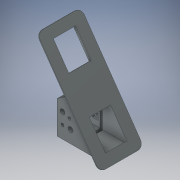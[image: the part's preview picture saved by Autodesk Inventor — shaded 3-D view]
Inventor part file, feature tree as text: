
AUTODESK INVENTOR PART (.ipt)
format: ipt  version: 2017 (Build 210142000, 142)  size: 451,072 bytes
history: native  units: mm
features: extrude x25, sketch x24, other x16, reference x6, fillet x2, hole x2, projected_geometry x2, shell x1
ambient origin geometry x8: Origin, YZ Plane, XZ Plane, XY Plane, X Axis, Y Axis, Z Axis, Center Point
bodies: Body1 (feature_tree)
feature tree (78):
  other  "Твердое тело1"
  extrude  "Выдавливание1"  Depth=2.4mm
  shell  "Оболочка1"  Thickness=1.7mm
  extrude  "Выдавливание7"  Depth=47.4mm
  extrude  "Выдавливание8"  Depth=25.2mm
  sketch  "Эскиз10"
  extrude  "Выдавливание9"  Depth=21.0mm TaperAngle=0.0deg
  extrude  "Выдавливание10"  Depth=6.108652mm
  extrude  "Выдавливание13"  Depth=2.5mm
  extrude  "Выдавливание14"  Depth=10.0mm
  fillet  "Сопряжение2"  Radius=3.8mm
  extrude  "Выдавливание15"  Depth=7.8mm
  extrude  "Выдавливание17"  Depth=2.0mm
  extrude  "Выдавливание18"  Depth=2.0mm
  extrude  "Выдавливание19"  Depth=2.9mm
  extrude  "Выдавливание20"  Depth=29.0mm TaperAngle=0.0deg
  extrude  "Выдавливание21"  Depth=6.108652mm
  extrude  "Выдавливание22"  Depth=28.6mm TaperAngle=0.0deg
  fillet  "Сопряжение4"  Radius=28.6mm
  extrude  "Выдавливание23"  Depth=28.6mm TaperAngle=0.0deg
  sketch  "Эскиз27"
  extrude  "Выдавливание24"  Depth=1.0mm
  extrude  "Выдавливание25"  Depth=8.0mm TaperAngle=0.0deg
  extrude  "Выдавливание26"  Depth=8.0mm TaperAngle=0.0deg
  sketch  "Эскиз31"
  extrude  "Выдавливание27"  Depth=6.0mm
  extrude  "Выдавливание28"  Depth=10.0mm TaperAngle=0.0deg
  hole  "Отверстие2"  [1 undecoded]
  hole  "Отверстие3"  [1 undecoded]
  sketch  "Эскиз32"
  sketch  "Эскиз33"
  other  "РабПлоскость4"
  sketch  "Эскиз35"
  other  "РабПлоскость5"
  sketch  "Эскиз36"
  extrude  "Выдавливание29"  Depth=10.0mm TaperAngle=0.0deg
  sketch  "Эскиз38"
  extrude  "Выдавливание30"  Depth=0.2mm TaperAngle=0.0deg
  extrude  "Выдавливание31"  Depth=6.0mm TaperAngle=0.0deg
  sketch  "Эскиз39"
  extrude  "Выдавливание32"  Depth=3.8mm TaperAngle=0.0deg
  extrude  "Выдавливание33"  Depth=3.8mm TaperAngle=0.0deg
  sketch  "Эскиз1"
  sketch  "Эскиз7"
  sketch  "Эскиз8"
  sketch  "Эскиз15"
  sketch  "Эскиз16"
  sketch  "Эскиз19"
  sketch  "Эскиз20"
  projected_geometry  "Спроецированная петля2"
  sketch  "Эскиз21"
  sketch  "Эскиз22"
  sketch  "Эскиз23"
  projected_geometry  "Спроецированная петля3"
  sketch  "Эскиз24"
  sketch  "Эскиз25"
  sketch  "Эскиз29"
  sketch  "Эскиз30"
  reference  "Ссылка1"
  reference  "Ссылка2"
  other  "РабПлоскость3"
  reference  "Ссылка4"
  reference  "Ссылка5"
  reference  "Ссылка6"
  reference  "Ссылка7"
  sketch  "Эскиз37"
  parser-record x2  (decoder bookkeeping rows leaked as tree rows — omitted from the tree; the rows remain in map.json)
  other  "Сборка1.iam"
  other  "Эскиз кожуха:1"
  other  "Frame0001_ЗЕРКАЛО:1"
  other  "GOST Угол 2 ГОСТ 8509-93 00000002_ЗЕРКАЛО:1"
  other  "Frame0001:1"
  other  "GOST Угол 2 ГОСТ 8509-93 00000005:1"
  other  "Frame0001_ЗЕРКАЛО4:1"
  other  "GOST Угол 2 ГОСТ 8509-93 00000005_ЗЕРКАЛО:1"
  other  "GOST Угол 2 ГОСТ 8509-93 00000003:1"
  other  "GOST Угол 2 ГОСТ 8509-93 00000004:1"
note: 2 required parameter values undecoded (feature->parameter linkage not recoverable at this tier; creation-order binding heuristic only, values carry confidence <= 0.55)
note: 2 file-system paths scrubbed to <path> (originals preserved in map.json)
